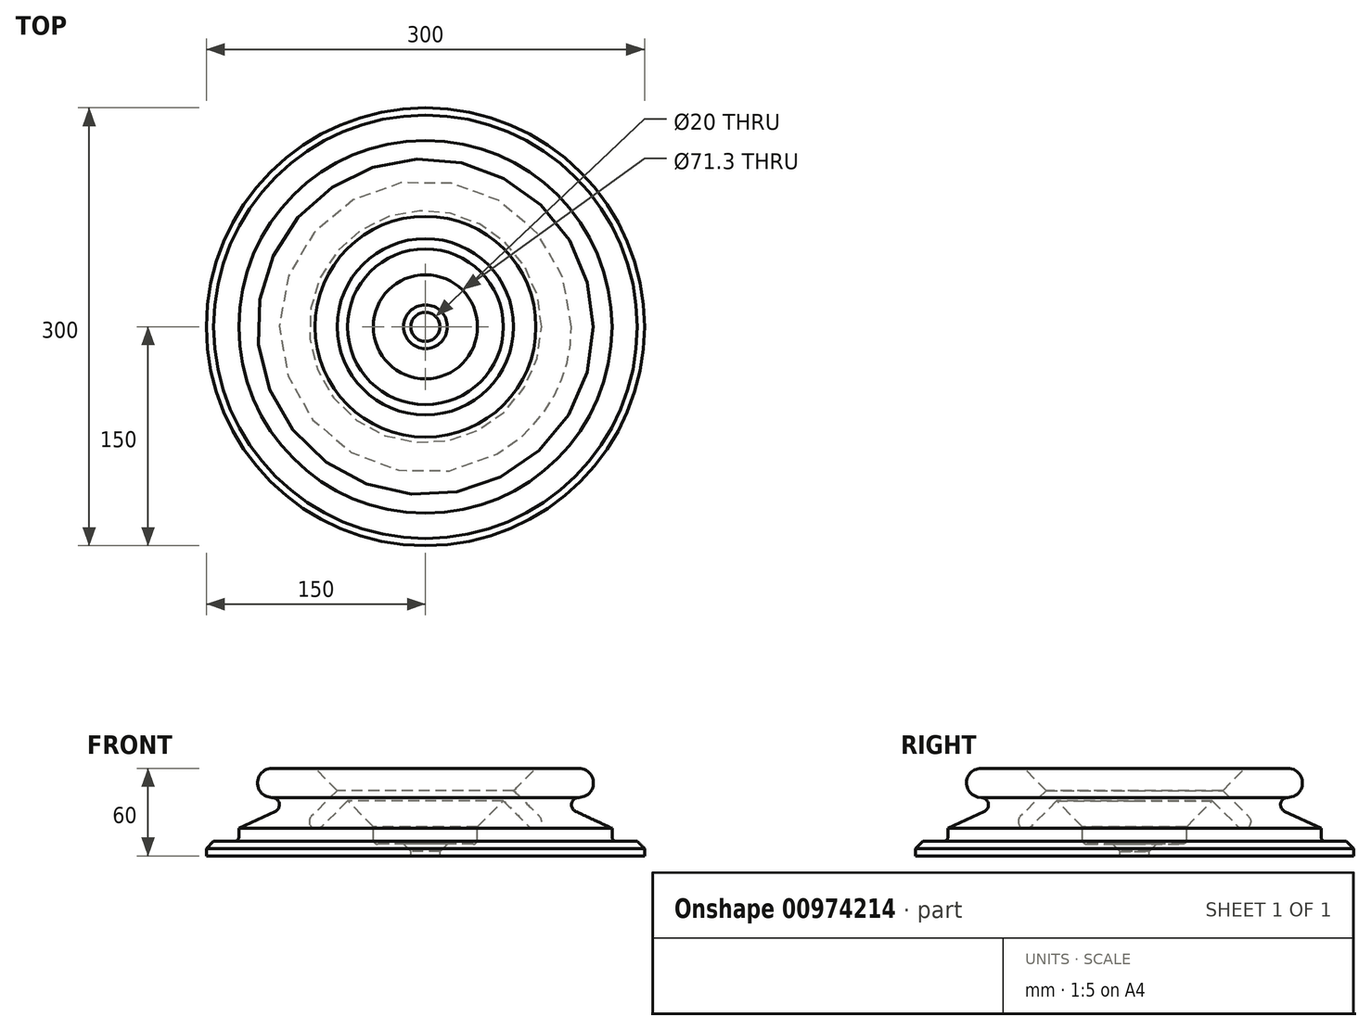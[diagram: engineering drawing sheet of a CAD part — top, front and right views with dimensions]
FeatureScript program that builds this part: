
annotation { "Feature Type Name" : "Feature", "Feature Type Description" : "" }
export const myFeature = defineFeature(function(context is Context, id is Id, definition is map)
    precondition{}
    {
        {
            var Q0;
            Q0=qCreatedBy(makeId("Front.planeOp"),FACE);
            var sketch = newSketch(context, id + "F0", { "sketchPlane" : qUnion([Q0])});
            skLineSegment(sketch, "E0", {"start": v(0, 50.08) * mm, "end": v(0, 0) * mm, "construction": true});
            skLineSegment(sketch, "E1", {"start": v(10, 0) * mm, "end": v(10, 3) * mm});
            skLineSegment(sketch, "E2", {"start": v(10, 3) * mm, "end": v(15, 8) * mm});
            skLineSegment(sketch, "E3", {"start": v(15, 8) * mm, "end": v(35.65, 8) * mm});
            skLineSegment(sketch, "E4", {"start": v(35.65, 8) * mm, "end": v(35.65, 20) * mm});
            skLineSegment(sketch, "E5", {"start": v(35.65, 20) * mm, "end": v(53.33, 37.68) * mm});
            skArc(sketch, "E6", {"start": v(71, 20) * mm, "mid": v(78.08, 20) * mm, "end": v(78.08, 27.07) * mm});
            skLineSegment(sketch, "E7", {"start": v(71, 20) * mm, "end": v(53.33, 37.68) * mm});
            skLineSegment(sketch, "E8", {"start": v(60.4, 44.75) * mm, "end": v(78.08, 27.07) * mm});
            skLineSegment(sketch, "E9", {"start": v(60.4, 44.75) * mm, "end": v(75.65, 60) * mm});
            skLineSegment(sketch, "E10", {"start": v(75.65, 60) * mm, "end": v(105, 60) * mm});
            skLineSegment(sketch, "E11", {"start": v(10, 0) * mm, "end": v(150, 0) * mm});
            skLineSegment(sketch, "E12", {"start": v(150, 0) * mm, "end": v(150, 5) * mm});
            skLineSegment(sketch, "E13", {"start": v(150, 5) * mm, "end": v(145, 10) * mm});
            skLineSegment(sketch, "E14", {"start": v(145, 10) * mm, "end": v(127.75, 10) * mm});
            skLineSegment(sketch, "E15", {"start": v(127.75, 10) * mm, "end": v(127.75, 18.87) * mm});
            skLineSegment(sketch, "E16", {"start": v(127.75, 18.87) * mm, "end": v(102.89, 30.47) * mm});
            skArc(sketch, "E17", {"start": v(105, 40) * mm, "mid": v(100.12, 36.08) * mm, "end": v(102.89, 30.47) * mm});
            skArc(sketch, "E18", {"start": v(105, 40) * mm, "mid": v(115, 50) * mm, "end": v(105, 60) * mm});
            skSolve(sketch);
        }
        {
            var Q0;
            Q0=makeQuery(id+"F0.imprint","IMPRINT",FACE,{"disambiguationData":[TD([[makeQuery(id+"F0.imprint","IMPRINT",EDGE,{"derivedFrom":sQuery(id+"F0.wireOp",EDGE,"E1")}),-1.0]])]});
            var Q1;
            Q1=sQuery(id+"F0.wireOp",EDGE,"E0");
            revolve(context, id + "F1", {"surfaceOperationType" : NewSurfaceOperationType.NEW, "entities" : qUnion([Q0]), "axis" : qUnion([Q1]), "revolveType" : RevolveType.FULL});
        }
        {
            var Q0;
            Q0=makeQuery(id+"F1.opRevolve","SWEPT_EDGE",EDGE,{"disambiguationData":[OSD([sQuery(id+"F0.wireOp",EDGE,"E3"),sQuery(id+"F0.wireOp",EDGE,"E4")])]});
            var Q1;
            Q1=makeQuery(id+"F1.opRevolve","SWEPT_EDGE",EDGE,{"disambiguationData":[OSD([sQuery(id+"F0.wireOp",EDGE,"E14"),sQuery(id+"F0.wireOp",EDGE,"E15")])]});
            fillet(context, id + "F2", {"entities" : qUnion([Q0, Q1]), "radius" : 3 * mm, "tangentPropagation" : true, "allowEdgeOverflow" : false});
        }
    });
